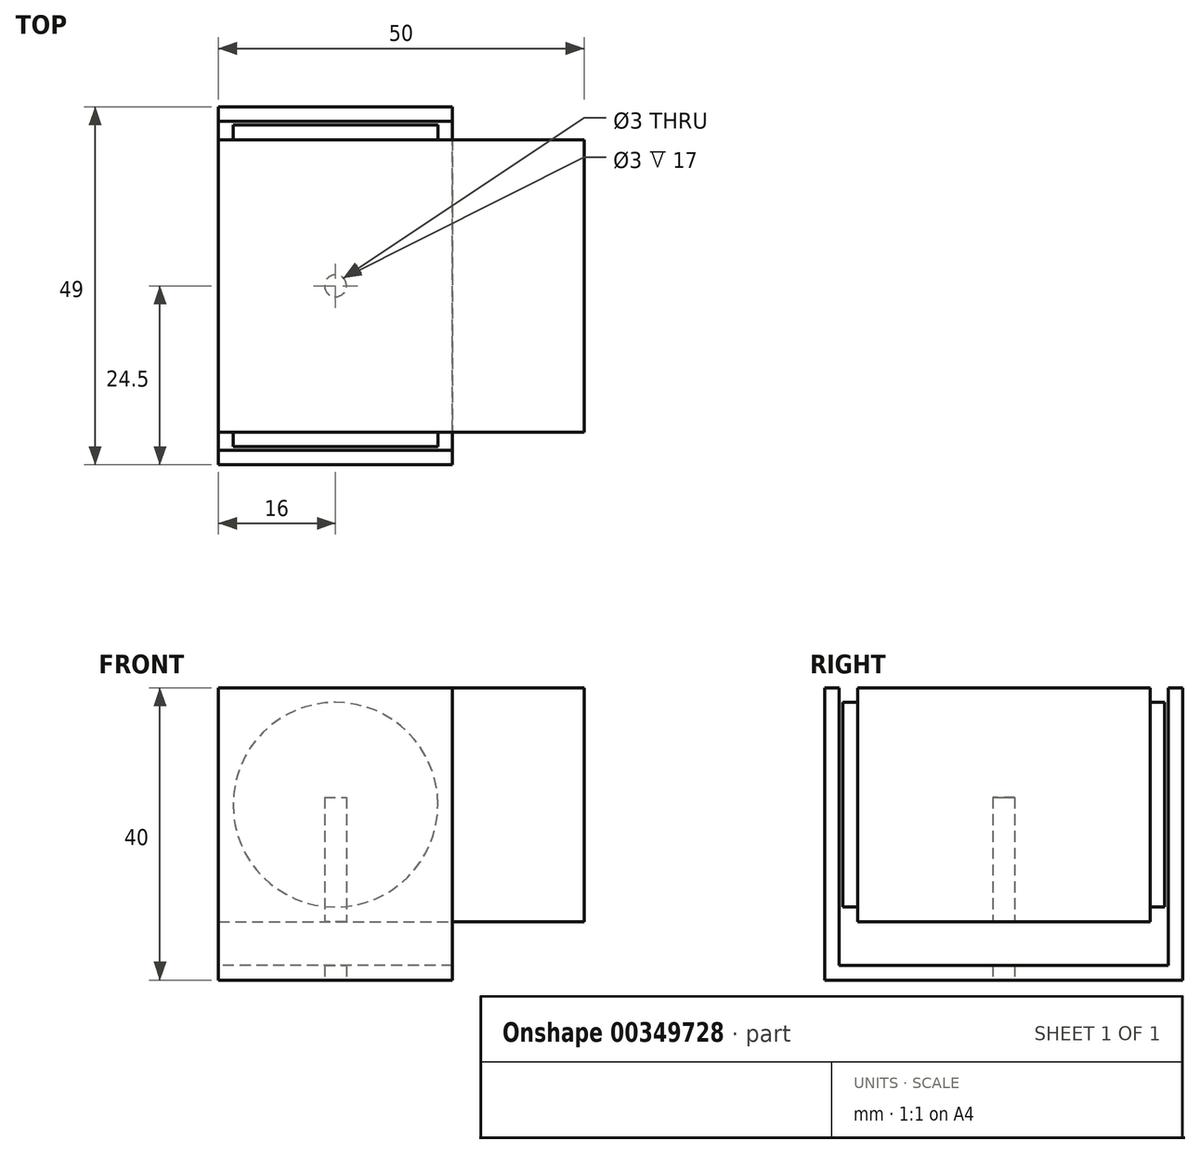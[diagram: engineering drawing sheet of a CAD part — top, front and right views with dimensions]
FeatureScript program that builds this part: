
annotation { "Feature Type Name" : "Feature", "Feature Type Description" : "" }
export const myFeature = defineFeature(function(context is Context, id is Id, definition is map)
    precondition{}
    {
        {
            var Q0;
            Q0=qCreatedBy(makeId("Front.planeOp"),FACE);
            var sketch = newSketch(context, id + "F0", { "sketchPlane" : qUnion([Q0])});
            skLineSegment(sketch, "E0.bottom", {"start": v(-25, 16) * mm, "end": v(25, 16) * mm});
            skLineSegment(sketch, "E0.top", {"start": v(-25, -16) * mm, "end": v(25, -16) * mm});
            skLineSegment(sketch, "E0.left", {"start": v(-25, 16) * mm, "end": v(-25, -16) * mm});
            skLineSegment(sketch, "E0.right", {"start": v(25, 16) * mm, "end": v(25, -16) * mm});
            skSolve(sketch);
        }
        {
            var Q0;
            Q0=makeQuery(id+"F0.imprint","IMPRINT",FACE,{"disambiguationData":[TD([[makeQuery(id+"F0.imprint","IMPRINT",EDGE,{"derivedFrom":sQuery(id+"F0.wireOp",EDGE,"E0.bottom")}),-1.0]])]});
            extrude(context, id + "F1", {"entities" : qUnion([Q0]), "depth" : 40 * mm});
        }
        {
            var Q0;
            Q0=makeQuery(id+"F1.opExtrude","CAP_FACE",FACE,{"disambiguationData":[OSD([sQuery(id+"F0.wireOp",EDGE,"E0.bottom"),sQuery(id+"F0.wireOp",EDGE,"E0.top"),sQuery(id+"F0.wireOp",EDGE,"E0.left"),sQuery(id+"F0.wireOp",EDGE,"E0.right")])],"isStart":false});
            var sketch = newSketch(context, id + "F2", { "sketchPlane" : qUnion([Q0])});
            skCircle(sketch, "E1", {"center": v(-9, 0) * mm, "radius": 14 * mm});
            skSolve(sketch);
        }
        {
            var Q0;
            Q0=makeQuery(id+"F2.imprint","IMPRINT",FACE,{"disambiguationData":[TD([[makeQuery(id+"F2.imprint","IMPRINT",EDGE,{"derivedFrom":sQuery(id+"F2.wireOp",EDGE,"E1")}),1.0]])]});
            extrude(context, id + "F3", {"entities" : qUnion([Q0]), "operationType" : NewBodyOperationType.ADD, "depth" : 2 * mm});
        }
        {
            var Q0;
            Q0=makeQuery(id+"F1.opExtrude","CAP_FACE",FACE,{"disambiguationData":[OSD([sQuery(id+"F0.wireOp",EDGE,"E0.bottom"),sQuery(id+"F0.wireOp",EDGE,"E0.top"),sQuery(id+"F0.wireOp",EDGE,"E0.left"),sQuery(id+"F0.wireOp",EDGE,"E0.right")])],"isStart":true});
            var sketch = newSketch(context, id + "F4", { "sketchPlane" : qUnion([Q0])});
            skCircle(sketch, "E2", {"center": v(9, 0) * mm, "radius": 14 * mm});
            skSolve(sketch);
        }
        {
            var Q0;
            Q0=makeQuery(id+"F4.imprint","IMPRINT",FACE,{"disambiguationData":[TD([[makeQuery(id+"F4.imprint","IMPRINT",EDGE,{"derivedFrom":sQuery(id+"F4.wireOp",EDGE,"E2")}),1.0]])]});
            extrude(context, id + "F5", {"entities" : qUnion([Q0]), "operationType" : NewBodyOperationType.ADD, "depth" : 2 * mm});
        }
        {
            var Q0;
            Q0=makeQuery(id+"F1.opExtrude","SWEPT_FACE",FACE,{"disambiguationData":[OSD([sQuery(id+"F0.wireOp",EDGE,"E0.left")])]});
            var sketch = newSketch(context, id + "F6", { "sketchPlane" : qUnion([Q0])});
            skLineSegment(sketch, "E3", {"start": v(-2.5, 16) * mm, "end": v(-2.5, -22) * mm});
            skLineSegment(sketch, "E4", {"start": v(-2.5, -22) * mm, "end": v(42.5, -22) * mm});
            skLineSegment(sketch, "E5", {"start": v(42.5, -22) * mm, "end": v(42.5, 16) * mm});
            skLineSegment(sketch, "E6", {"start": v(42.5, 16) * mm, "end": v(44.5, 16) * mm});
            skLineSegment(sketch, "E7", {"start": v(44.5, 16) * mm, "end": v(44.5, -24) * mm});
            skLineSegment(sketch, "E8", {"start": v(44.5, -24) * mm, "end": v(-4.5, -24) * mm});
            skLineSegment(sketch, "E9", {"start": v(-4.5, -24) * mm, "end": v(-4.5, 16) * mm});
            skLineSegment(sketch, "E10", {"start": v(-4.5, 16) * mm, "end": v(-2.5, 16) * mm});
            skSolve(sketch);
        }
        {
            var Q0;
            Q0=makeQuery(id+"F6.imprint","IMPRINT",FACE,{"disambiguationData":[TD([[makeQuery(id+"F6.imprint","IMPRINT",EDGE,{"derivedFrom":sQuery(id+"F6.wireOp",EDGE,"E3")}),-1.0]])]});
            extrude(context, id + "F7", {"entities" : qUnion([Q0]), "oppositeDirection" : true, "depth" : 32 * mm});
        }
        {
            var Q0;
            Q0=makeQuery(id+"F7.opExtrude","SWEPT_FACE",FACE,{"disambiguationData":[OSD([sQuery(id+"F6.wireOp",EDGE,"E8")])]});
            var sketch = newSketch(context, id + "F8", { "sketchPlane" : qUnion([Q0])});
            skCircle(sketch, "E11", {"center": v(-9, 20) * mm, "radius": 1.5 * mm});
            skSolve(sketch);
        }
        {
            var Q0;
            Q0=makeQuery(id+"F8.imprint","IMPRINT",FACE,{"disambiguationData":[TD([[makeQuery(id+"F8.imprint","IMPRINT",EDGE,{"derivedFrom":sQuery(id+"F8.wireOp",EDGE,"E11")}),1.0]])]});
            extrude(context, id + "F9", {"entities" : qUnion([Q0]), "operationType" : NewBodyOperationType.REMOVE, "oppositeDirection" : true, "depth" : 25 * mm});
        }
    });
